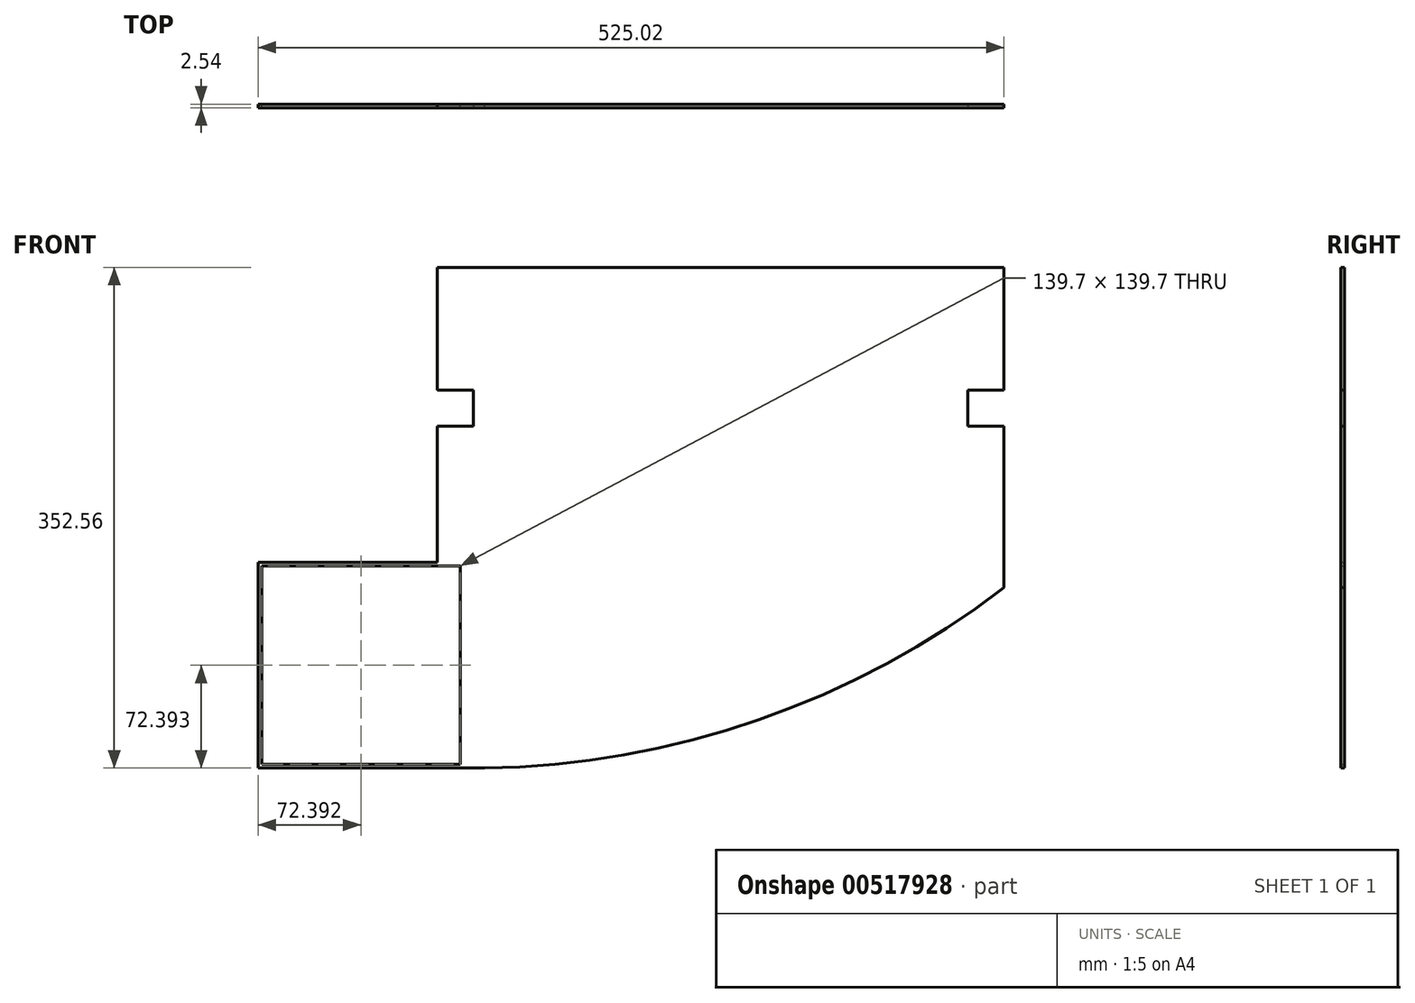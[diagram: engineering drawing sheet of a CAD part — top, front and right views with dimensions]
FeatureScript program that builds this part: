
annotation { "Feature Type Name" : "Feature", "Feature Type Description" : "" }
export const myFeature = defineFeature(function(context is Context, id is Id, definition is map)
    precondition{}
    {
        {
            var Q0;
            Q0=qCreatedBy(makeId("Front.planeOp"),FACE);
            var sketch = newSketch(context, id + "F0", { "sketchPlane" : qUnion([Q0])});
            skLineSegment(sketch, "E0", {"start": v(-98.06, 79.2) * mm, "end": v(300.72, 79.2) * mm});
            skLineSegment(sketch, "E1", {"start": v(300.72, 79.2) * mm, "end": v(300.72, -273.35) * mm});
            skLineSegment(sketch, "E2", {"start": v(300.72, -273.35) * mm, "end": v(-224.3, -273.35) * mm});
            skLineSegment(sketch, "E3", {"start": v(-224.3, -273.35) * mm, "end": v(-224.3, -128.57) * mm});
            skLineSegment(sketch, "E4", {"start": v(-224.3, -128.57) * mm, "end": v(-98.06, -128.57) * mm});
            skLineSegment(sketch, "E5", {"start": v(-98.06, -128.57) * mm, "end": v(-98.06, 79.2) * mm});
            skLineSegment(sketch, "E6", {"start": v(-82.06, -131.1) * mm, "end": v(-221.76, -131.1) * mm});
            skLineSegment(sketch, "E7", {"start": v(-221.76, -131.1) * mm, "end": v(-221.76, -270.8) * mm});
            skLineSegment(sketch, "E8", {"start": v(-221.76, -270.8) * mm, "end": v(-82.06, -270.8) * mm});
            skLineSegment(sketch, "E9", {"start": v(-82.06, -270.8) * mm, "end": v(-82.06, -131.1) * mm});
            skPoint(sketch, "E10", {"position": v(300.72, -146.35) * mm});
            skArc(sketch, "E11", {"start": v(-82.06, -273.35) * mm, "mid": v(120.05, -242.15) * mm, "end": v(300.72, -146.35) * mm});
            skSolve(sketch);
        }
        {
            var Q0;
            Q0=makeQuery(id+"F0.imprint","IMPRINT",FACE,{"disambiguationData":[TD([[makeQuery(id+"F0.imprint","IMPRINT",EDGE,{"derivedFrom":sQuery(id+"F0.wireOp",EDGE,"E0")}),-1.0]])]});
            extrude(context, id + "F1", {"entities" : qUnion([Q0]), "depth" : 2.54 * mm, "offsetDistance" : 25.4 * mm});
        }
        {
            var Q0;
            Q0=makeQuery(id+"F1.opExtrude","CAP_FACE",FACE,{"disambiguationData":[OSD([sQuery(id+"F0.wireOp",EDGE,"E0"),sQuery(id+"F0.wireOp",EDGE,"E1"),sQuery(id+"F0.wireOp",EDGE,"E2"),sQuery(id+"F0.wireOp",EDGE,"E3"),sQuery(id+"F0.wireOp",EDGE,"E4"),sQuery(id+"F0.wireOp",EDGE,"E5"),sQuery(id+"F0.wireOp",EDGE,"E6"),sQuery(id+"F0.wireOp",EDGE,"E7"),sQuery(id+"F0.wireOp",EDGE,"E8"),sQuery(id+"F0.wireOp",EDGE,"E9"),sQuery(id+"F0.wireOp",EDGE,"E11")])],"isStart":false});
            var sketch = newSketch(context, id + "F2", { "sketchPlane" : qUnion([Q0])});
            skLineSegment(sketch, "E12", {"start": v(-98.06, -7.15) * mm, "end": v(-72.66, -7.15) * mm});
            skLineSegment(sketch, "E13", {"start": v(-72.66, -7.15) * mm, "end": v(-72.66, -32.55) * mm});
            skLineSegment(sketch, "E14", {"start": v(-72.66, -32.55) * mm, "end": v(-98.06, -32.55) * mm});
            skLineSegment(sketch, "E15", {"start": v(-98.06, -32.55) * mm, "end": v(-98.06, -7.15) * mm});
            skSolve(sketch);
        }
        {
            var Q0;
            Q0=makeQuery(id+"F2.imprint","IMPRINT",FACE,{"disambiguationData":[TD([[makeQuery(id+"F2.imprint","IMPRINT",EDGE,{"derivedFrom":sQuery(id+"F2.wireOp",EDGE,"E12")}),-1.0]])]});
            extrude(context, id + "F3", {"entities" : qUnion([Q0]), "operationType" : NewBodyOperationType.REMOVE, "oppositeDirection" : true, "depth" : 25.4 * mm, "offsetDistance" : 25.4 * mm});
        }
        {
            var Q0;
            Q0=makeQuery(id+"F1.opExtrude","CAP_FACE",FACE,{"disambiguationData":[OSD([sQuery(id+"F0.wireOp",EDGE,"E0"),sQuery(id+"F0.wireOp",EDGE,"E1"),sQuery(id+"F0.wireOp",EDGE,"E2"),sQuery(id+"F0.wireOp",EDGE,"E3"),sQuery(id+"F0.wireOp",EDGE,"E4"),sQuery(id+"F0.wireOp",EDGE,"E5"),sQuery(id+"F0.wireOp",EDGE,"E6"),sQuery(id+"F0.wireOp",EDGE,"E7"),sQuery(id+"F0.wireOp",EDGE,"E8"),sQuery(id+"F0.wireOp",EDGE,"E9"),sQuery(id+"F0.wireOp",EDGE,"E11")])],"isStart":false});
            var sketch = newSketch(context, id + "F4", { "sketchPlane" : qUnion([Q0])});
            skLineSegment(sketch, "E16", {"start": v(300.72, -7.15) * mm, "end": v(275.32, -7.15) * mm});
            skLineSegment(sketch, "E17", {"start": v(275.32, -7.15) * mm, "end": v(275.32, -32.55) * mm});
            skLineSegment(sketch, "E18", {"start": v(275.32, -32.55) * mm, "end": v(300.72, -32.55) * mm});
            skSolve(sketch);
        }
        {
            var Q0;
            {var subQ0=sQuery(id+"F4.wireOp",EDGE,"E16");Q0=makeQuery(id+"F4.imprint","IMPRINT",FACE,{"disambiguationData":[TD([[makeQuery(id+"F4.imprint","IMPRINT",EDGE,{"derivedFrom":subQ0}),1.0]])]});}
            extrude(context, id + "F5", {"entities" : qUnion([Q0]), "operationType" : NewBodyOperationType.REMOVE, "oppositeDirection" : true, "depth" : 25.4 * mm, "offsetDistance" : 25.4 * mm});
        }
    });
